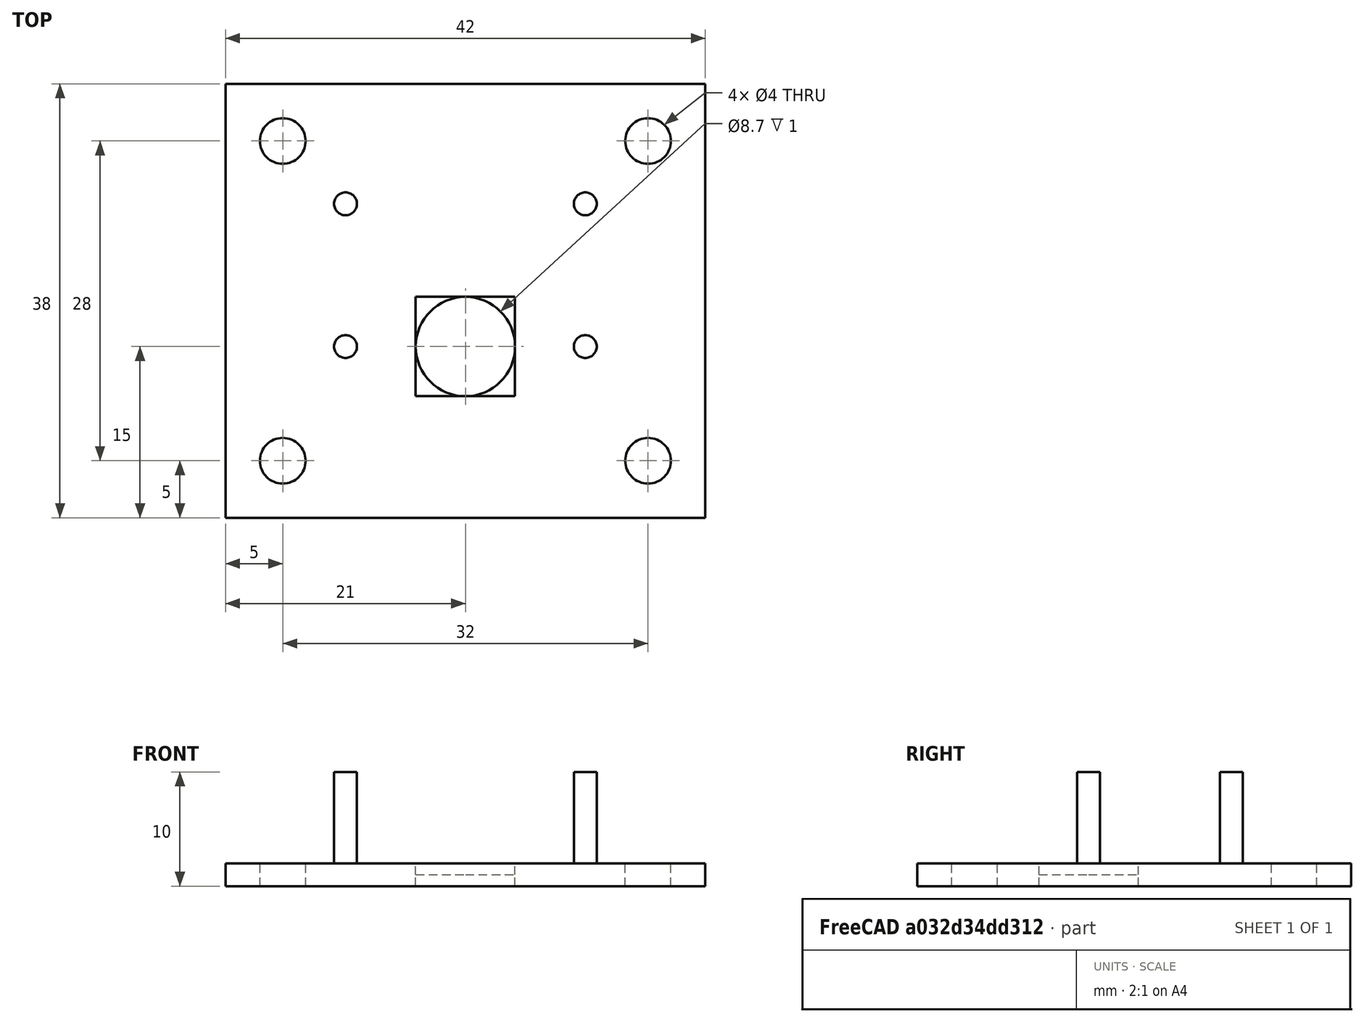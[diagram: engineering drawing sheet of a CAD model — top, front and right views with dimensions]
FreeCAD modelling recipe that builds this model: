
FCSTD DOCUMENT  (FreeCAD 0.18.1R)
Label: camfront
License: CC-BY 3.0
LicenseURL: http://creativecommons.org/licenses/by/3.0/
objects: Part::Cylinder×9, Part::Cut×6, Part::Box×2, Part::MultiFuse×1
note: 18 computed .brp shape members not serialized (recipe doc carries the construction recipe); baked Part::Feature solids carry a one-line shape summary decoded from their .brp

FEATURE [Part::Cylinder] Cylinder
  Angle = 360
  AttacherType = Attacher::AttachEngine3D
  Height = 10
  Placement = pos=(0,0,-3) rot=(0,0,1;0rad)
  Radius = 4.35
FEATURE [Part::Cylinder] Cylinder001  label="screw support"
  Angle = 360
  AttacherType = Attacher::AttachEngine3D
  Height = 10
  Placement = pos=(-10.5,0,0) rot=(0,0,1;0rad)
  Radius = 1
FEATURE [Part::Cylinder] Cylinder002  label="screw support001"
  Angle = 360
  AttacherType = Attacher::AttachEngine3D
  Height = 10
  Placement = pos=(10.5,0,0) rot=(0,0,1;0rad)
  Radius = 1
FEATURE [Part::Cylinder] Cylinder003  label="screw support002"
  Angle = 360
  AttacherType = Attacher::AttachEngine3D
  Height = 10
  Placement = pos=(-10.5,12.5,0) rot=(0,0,1;0rad)
  Radius = 1
FEATURE [Part::Cylinder] Cylinder004  label="screw support003"
  Angle = 360
  AttacherType = Attacher::AttachEngine3D
  Height = 10
  Placement = pos=(10.5,12.5,0) rot=(0,0,1;0rad)
  Radius = 1
FEATURE [Part::Box] Box  label="Cube"
  AttacherType = Attacher::AttachEngine3D
  Height = 2
  Length = 8.7
  Placement = pos=(-4.35,-4.35,1) rot=(0,0,1;0rad)
  Width = 8.7
FEATURE [Part::Cylinder] Cylinder005  label="BoltHole"
  Angle = 360
  AttacherType = Attacher::AttachEngine3D
  Height = 10
  Placement = pos=(-16,-10,0) rot=(0,0,1;0rad)
  Radius = 2
FEATURE [Part::Cylinder] Cylinder006  label="BoltHole001"
  Angle = 360
  AttacherType = Attacher::AttachEngine3D
  Height = 10
  Placement = pos=(16,18,0) rot=(0,0,1;0rad)
  Radius = 2
FEATURE [Part::Cylinder] Cylinder007  label="BoltHole002"
  Angle = 360
  AttacherType = Attacher::AttachEngine3D
  Height = 10
  Placement = pos=(16,-10,0) rot=(0,0,1;0rad)
  Radius = 2
FEATURE [Part::Cylinder] Cylinder008  label="BoltHole003"
  Angle = 360
  AttacherType = Attacher::AttachEngine3D
  Height = 10
  Placement = pos=(-16,18,0) rot=(0,0,1;0rad)
  Radius = 2
FEATURE [Part::Box] Box001  label="Cube001"
  AttacherType = Attacher::AttachEngine3D
  Height = 2
  Length = 42
  Placement = pos=(-21,-15,0) rot=(0,0,1;0rad)
  Width = 38
FEATURE [Part::Cut] Cut
  Base = -> Box001
  Tool = -> Box
FEATURE [Part::Cut] Cut001
  Base = -> Cut
  Tool = -> Cylinder
FEATURE [Part::Cut] Cut002
  Base = -> Cut001
  Tool = -> Cylinder008
FEATURE [Part::Cut] Cut003
  Base = -> Cut002
  Tool = -> Cylinder007
FEATURE [Part::Cut] Cut004
  Base = -> Cut003
  Tool = -> Cylinder006
FEATURE [Part::Cut] Cut005
  Base = -> Cut004
  Tool = -> Cylinder005
FEATURE [Part::MultiFuse] Fusion  label="fusion-camfront"
  Shapes = -> [Cylinder001,Cylinder002,Cylinder003,Cylinder004,Cut005]
